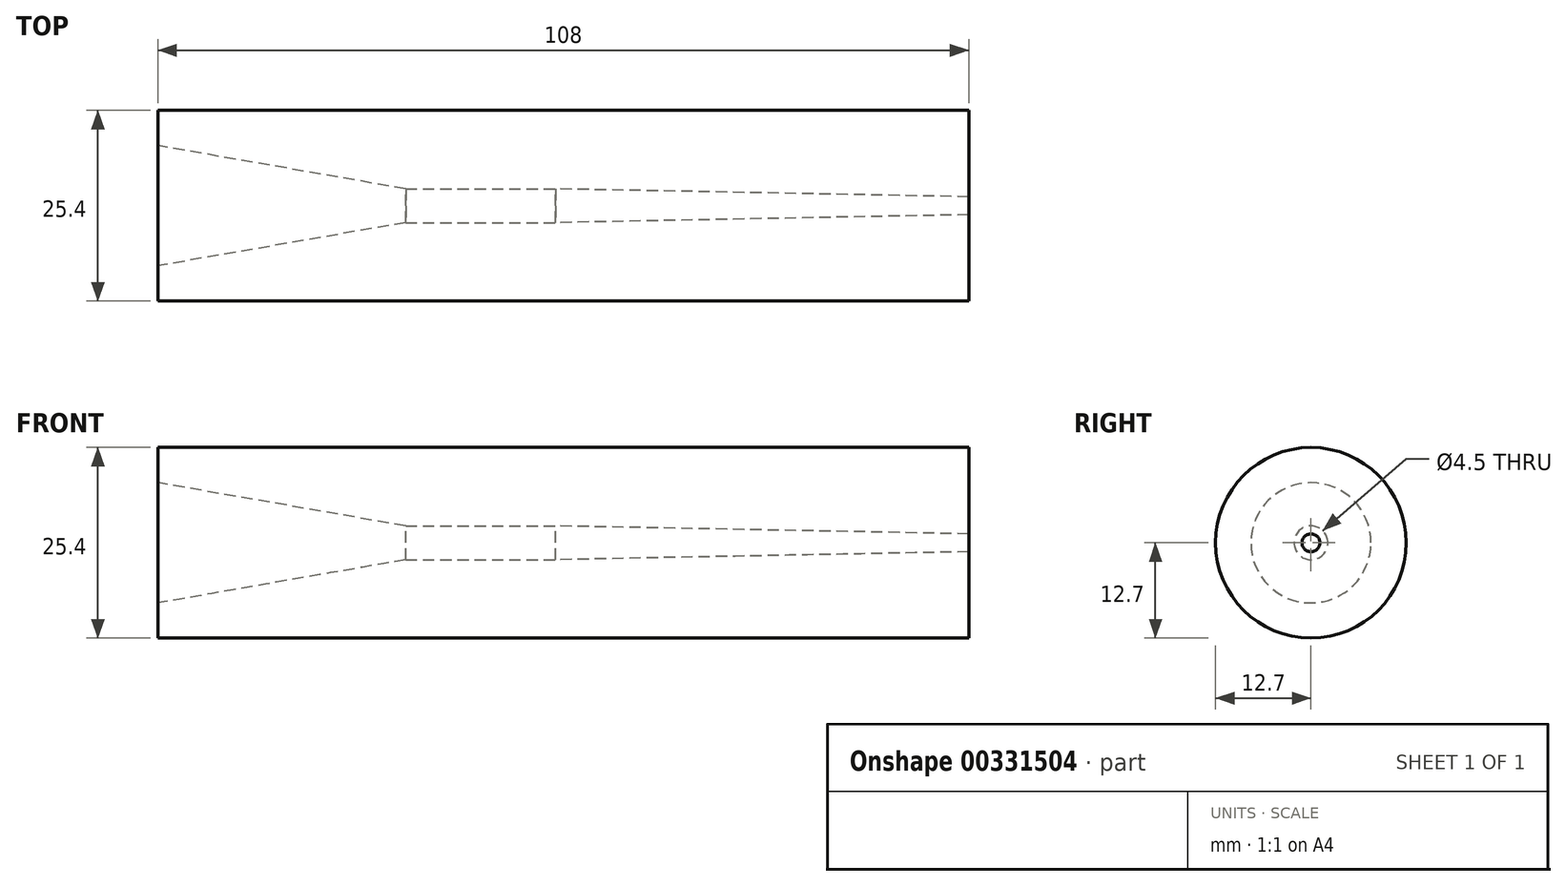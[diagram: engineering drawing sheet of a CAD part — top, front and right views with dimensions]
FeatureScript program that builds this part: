
annotation { "Feature Type Name" : "Feature", "Feature Type Description" : "" }
export const myFeature = defineFeature(function(context is Context, id is Id, definition is map)
    precondition{}
    {
        {
            var Q0;
            Q0=qCreatedBy(makeId("Front.planeOp"),FACE);
            var sketch = newSketch(context, id + "F0", { "sketchPlane" : qUnion([Q0])});
            skLineSegment(sketch, "E0", {"start": v(0, 0) * mm, "end": v(65, 0) * mm});
            skLineSegment(sketch, "E1", {"start": v(65, 0) * mm, "end": v(65, 1.2) * mm});
            skLineSegment(sketch, "E2", {"start": v(65, 1.2) * mm, "end": v(10, 2.25) * mm});
            skLineSegment(sketch, "E3", {"start": v(10, 2.25) * mm, "end": v(0, 2.25) * mm});
            skLineSegment(sketch, "E4", {"start": v(0, 2.25) * mm, "end": v(-10, 2.25) * mm});
            skLineSegment(sketch, "E5", {"start": v(-10, 2.25) * mm, "end": v(-43, 8) * mm});
            skLineSegment(sketch, "E6", {"start": v(-43, 8) * mm, "end": v(-43, 0) * mm});
            skLineSegment(sketch, "E7", {"start": v(-43, 0) * mm, "end": v(0, 0) * mm});
            skSolve(sketch);
        }
        {
            var Q0;
            Q0=qCreatedBy(makeId("Right.planeOp"),FACE);
            var sketch = newSketch(context, id + "F1", { "sketchPlane" : qUnion([Q0])});
            skCircle(sketch, "E8", {"center": v(0, 0) * mm, "radius": 12.7 * mm});
            skSolve(sketch);
        }
        {
            var Q0;
            Q0 = qSketchRegion(id + "F1", true);
            extrude(context, id + "F2", {"entities" : qUnion([Q0]), "depth" : 65 * mm, "hasSecondDirection" : true, "secondDirectionOppositeDirection" : true, "secondDirectionDepth" : 43 * mm});
        }
        {
            var Q0;
            Q0 = qSketchRegion(id + "F0", true);
            var Q1;
            Q1=sQuery(id+"F0.wireOp",EDGE,"E7");
            revolve(context, id + "F3", {"operationType" : NewBodyOperationType.REMOVE, "entities" : qUnion([Q0]), "axis" : qUnion([Q1]), "revolveType" : RevolveType.FULL, "oppositeDirection" : true});
        }
    });
